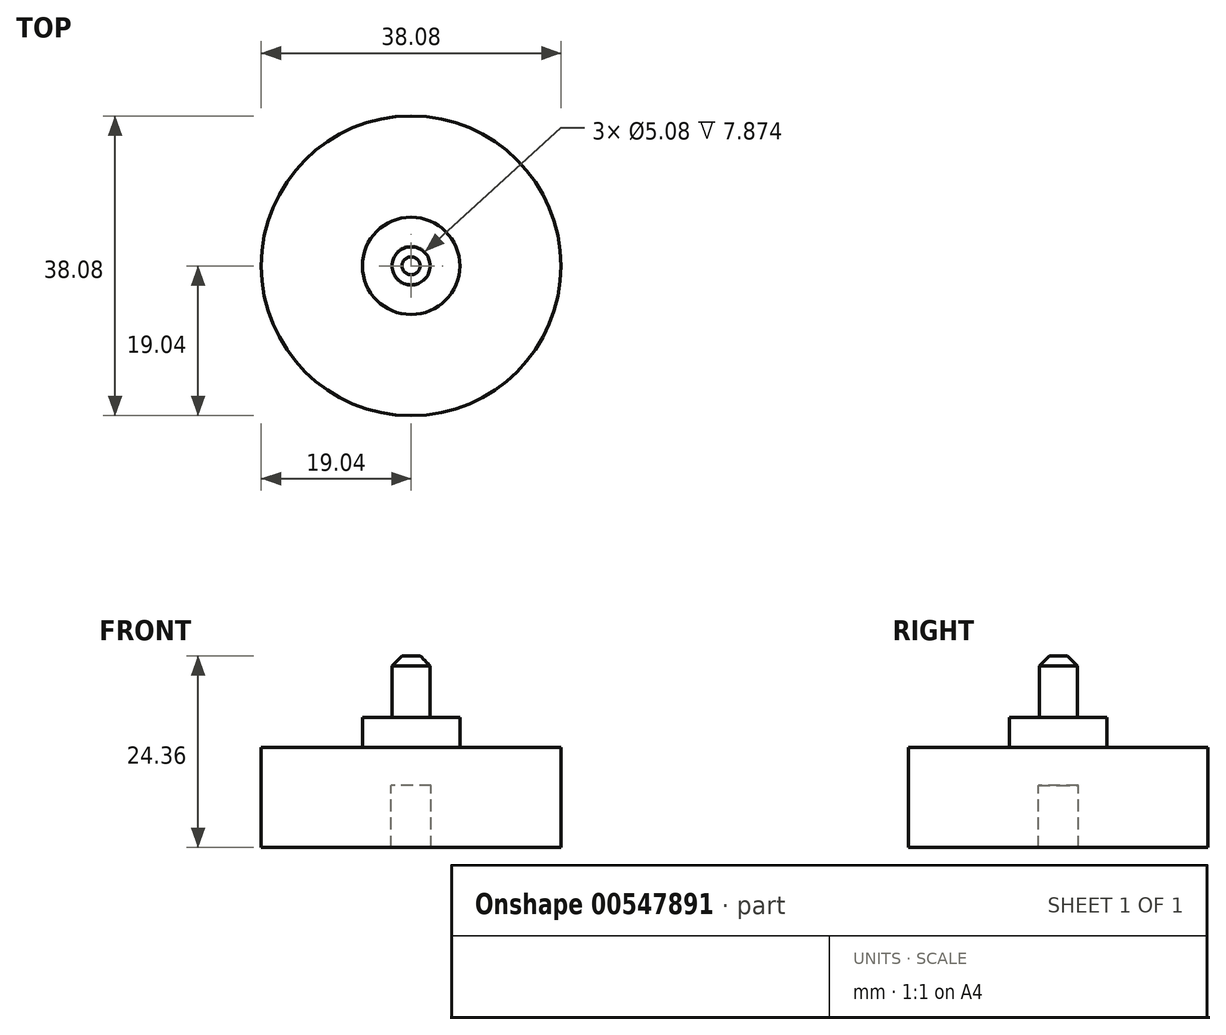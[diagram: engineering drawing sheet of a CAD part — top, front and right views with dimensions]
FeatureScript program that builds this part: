
annotation { "Feature Type Name" : "Feature", "Feature Type Description" : "" }
export const myFeature = defineFeature(function(context is Context, id is Id, definition is map)
    precondition{}
    {
        {
            var Q0;
            Q0=qCreatedBy(makeId("Front.planeOp"),FACE);
            var sketch = newSketch(context, id + "F0", { "sketchPlane" : qUnion([Q0])});
            skLineSegment(sketch, "E0", {"start": v(19.04, 0) * mm, "end": v(19.04, 12.7) * mm});
            skLineSegment(sketch, "E1", {"start": v(6.18, 16.51) * mm, "end": v(6.18, 12.7) * mm});
            skLineSegment(sketch, "E2", {"start": v(19.04, 12.7) * mm, "end": v(6.18, 12.7) * mm});
            skLineSegment(sketch, "E3", {"start": v(2.54, 0) * mm, "end": v(2.54, 7.87) * mm});
            skLineSegment(sketch, "E4", {"start": v(2.54, 7.87) * mm, "end": v(0, 7.87) * mm});
            skPoint(sketch, "E4.endSnap0", {"position": v(0, 12.18) * mm});
            skLineSegment(sketch, "E5", {"start": v(19.04, 0) * mm, "end": v(2.54, 0) * mm});
            skLineSegment(sketch, "E6", {"start": v(0, 24.36) * mm, "end": v(0, 7.87) * mm});
            skLineSegment(sketch, "E7", {"start": v(0, 24.36) * mm, "end": v(2.41, 24.36) * mm});
            skLineSegment(sketch, "E8", {"start": v(2.41, 24.36) * mm, "end": v(2.41, 16.51) * mm});
            skLineSegment(sketch, "E9", {"start": v(6.18, 16.51) * mm, "end": v(2.41, 16.51) * mm});
            skSolve(sketch);
        }
        {
            var Q0;
            Q0 = qSketchRegion(id + "F0", true);
            var Q1;
            Q1=sQuery(id+"F0.wireOp",EDGE,"E6");
            revolve(context, id + "F1", {"entities" : qUnion([Q0]), "axis" : qUnion([Q1]), "revolveType" : RevolveType.FULL});
        }
        {
            var Q0;
            Q0=makeQuery(id+"F1.opRevolve","SWEPT_EDGE",EDGE,{"disambiguationData":[OSD([sQuery(id+"F0.wireOp",EDGE,"E7"),sQuery(id+"F0.wireOp",EDGE,"E8")])]});
            chamfer(context, id + "F2", {"entities" : qUnion([Q0]), "width" : 1.27 * mm, "tangentPropagation" : true});
        }
    });
